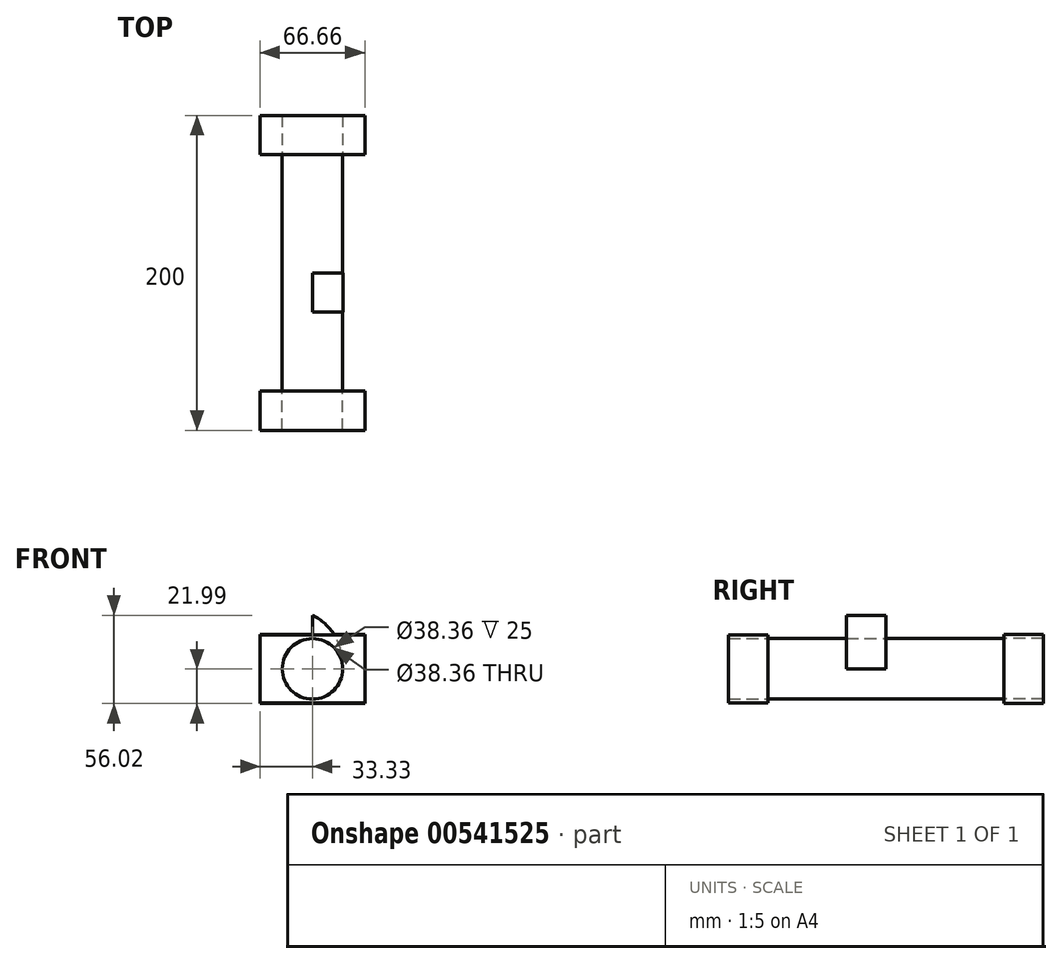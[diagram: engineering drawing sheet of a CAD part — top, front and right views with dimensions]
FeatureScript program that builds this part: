
annotation { "Feature Type Name" : "Feature", "Feature Type Description" : "" }
export const myFeature = defineFeature(function(context is Context, id is Id, definition is map)
    precondition{}
    {
        {
            var Q0;
            Q0=qCreatedBy(makeId("Front.planeOp"),FACE);
            var sketch = newSketch(context, id + "F0", { "sketchPlane" : qUnion([Q0])});
            skCircle(sketch, "E0", {"center": v(0, 0) * mm, "radius": 19.18 * mm});
            skLineSegment(sketch, "E1", {"start": v(0, 19.18) * mm, "end": v(0, 34.03) * mm});
            skArc(sketch, "E2", {"start": v(19.18, 0) * mm, "mid": v(14.85, 19.98) * mm, "end": v(0, 34.03) * mm});
            skSolve(sketch);
        }
        {
            var Q0;
            {var subQ0=sQuery(id+"F0.wireOp",EDGE,"E0");var subQ1=makeQuery(id+"F0.imprint","INTERSECT",VERTEX,{"derivedFrom":[subQ0,sQuery(id+"F0.wireOp",EDGE,"E1")]});Q0=makeQuery(id+"F0.imprint","IMPRINT",FACE,{"disambiguationData":[TD([[makeQuery(id+"F0.imprint","IMPRINT",EDGE,{"disambiguationData":[TD([[subQ1,1.0]])],"derivedFrom":subQ0}),1.0]])]});}
            extrude(context, id + "F1", {"entities" : qUnion([Q0]), "endBound" : BoundingType.SYMMETRIC, "depth" : 150 * mm, "offsetDistance" : 25 * mm});
        }
        {
            var Q0;
            Q0=qSketchRegion(id+"F0",true);
            extrude(context, id + "F2", {"entities" : qUnion([Q0]), "operationType" : NewBodyOperationType.ADD, "depth" : 25 * mm, "offsetDistance" : 25 * mm});
        }
        {
            var Q0;
            Q0=makeQuery(id+"F1.opExtrude","CAP_FACE",FACE,{"disambiguationData":[OSD([sQuery(id+"F0.wireOp",EDGE,"E0")])],"isStart":false});
            var sketch = newSketch(context, id + "F3", { "sketchPlane" : qUnion([Q0])});
            skLineSegment(sketch, "E3.bottom", {"start": v(-33.26, 21.47) * mm, "end": v(33.26, 21.47) * mm});
            skLineSegment(sketch, "E3.top", {"start": v(-33.26, -21.47) * mm, "end": v(33.26, -21.47) * mm});
            skLineSegment(sketch, "E3.left", {"start": v(-33.26, 21.47) * mm, "end": v(-33.26, -21.47) * mm});
            skLineSegment(sketch, "E3.right", {"start": v(33.26, 21.47) * mm, "end": v(33.26, -21.47) * mm});
            skPoint(sketch, "E3.middle", {"position": v(0, 0) * mm});
            skSolve(sketch);
        }
        {
            var Q0;
            Q0=makeQuery(id+"F3.imprint","IMPRINT",FACE,{"disambiguationData":[TD([[makeQuery(id+"F3.imprint","IMPRINT",EDGE,{"derivedFrom":sQuery(id+"F3.wireOp",EDGE,"E3.bottom")}),-1.0]])]});
            extrude(context, id + "F4", {"entities" : qUnion([Q0]), "depth" : 25 * mm, "offsetDistance" : 25 * mm});
        }
        {
            var Q0;
            Q0=makeQuery(id+"F1.opExtrude","CAP_FACE",FACE,{"disambiguationData":[OSD([sQuery(id+"F0.wireOp",EDGE,"E0")])],"isStart":true});
            var sketch = newSketch(context, id + "F5", { "sketchPlane" : qUnion([Q0])});
            skLineSegment(sketch, "E4.bottom", {"start": v(-33.33, 22) * mm, "end": v(33.33, 22) * mm});
            skLineSegment(sketch, "E4.top", {"start": v(-33.33, -22) * mm, "end": v(33.33, -22) * mm});
            skLineSegment(sketch, "E4.left", {"start": v(-33.33, 22) * mm, "end": v(-33.33, -22) * mm});
            skLineSegment(sketch, "E4.right", {"start": v(33.33, 22) * mm, "end": v(33.33, -22) * mm});
            skPoint(sketch, "E4.middle", {"position": v(0, 0) * mm});
            skSolve(sketch);
        }
        {
            var Q0;
            Q0=makeQuery(id+"F5.imprint","IMPRINT",FACE,{"disambiguationData":[TD([[makeQuery(id+"F5.imprint","IMPRINT",EDGE,{"derivedFrom":sQuery(id+"F5.wireOp",EDGE,"E4.bottom")}),-1.0]])]});
            extrude(context, id + "F6", {"entities" : qUnion([Q0]), "depth" : 25 * mm, "offsetDistance" : 25 * mm});
        }
    });
